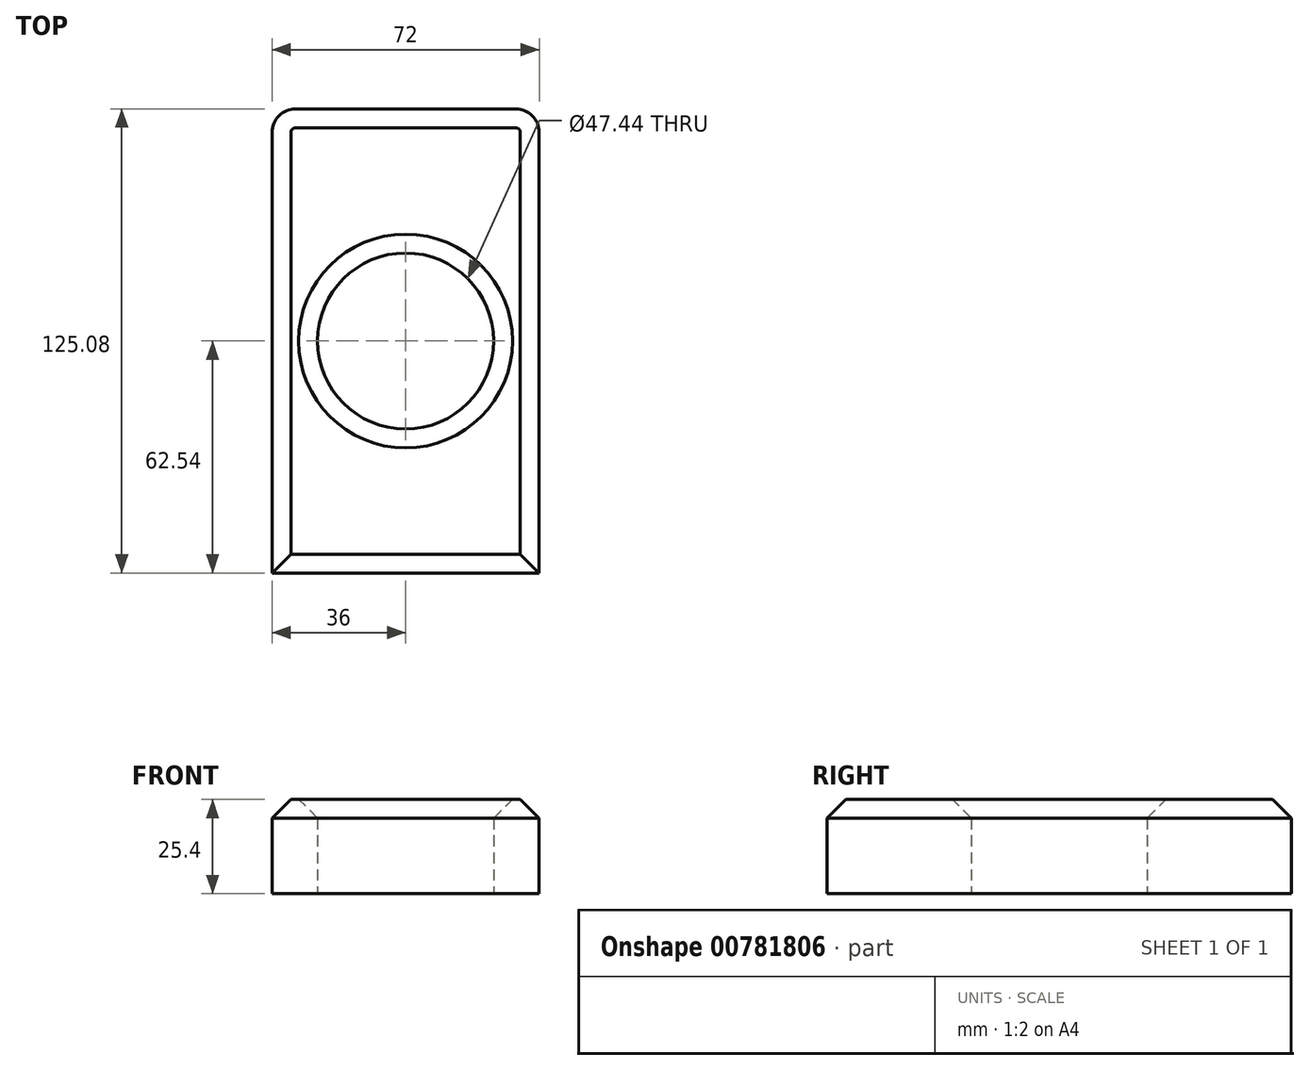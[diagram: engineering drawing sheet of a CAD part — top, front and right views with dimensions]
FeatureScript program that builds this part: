
annotation { "Feature Type Name" : "Feature", "Feature Type Description" : "" }
export const myFeature = defineFeature(function(context is Context, id is Id, definition is map)
    precondition{}
    {
        {
            var Q0;
            Q0=qCreatedBy(makeId("Top.planeOp"),FACE);
            var sketch = newSketch(context, id + "F0", { "sketchPlane" : qUnion([Q0])});
            skLineSegment(sketch, "E0.bottom", {"start": v(36, -62.54) * mm, "end": v(-36, -62.54) * mm});
            skLineSegment(sketch, "E0.top", {"start": v(29.65, 62.54) * mm, "end": v(-29.65, 62.54) * mm});
            skLineSegment(sketch, "E0.left", {"start": v(36, -62.54) * mm, "end": v(36, 56.2) * mm});
            skLineSegment(sketch, "E0.right", {"start": v(-36, -62.54) * mm, "end": v(-36, 56.2) * mm});
            skPoint(sketch, "E0.middle", {"position": v(0, 0) * mm});
            skPoint(sketch, "E1.visualSharp", {"position": v(36, 62.54) * mm});
            skArc(sketch, "E1.filletArc", {"start": v(36, 56.2) * mm, "mid": v(34.14, 60.68) * mm, "end": v(29.65, 62.54) * mm});
            skPoint(sketch, "E2.visualSharp", {"position": v(-36, 62.54) * mm});
            skArc(sketch, "E2.filletArc", {"start": v(-29.65, 62.54) * mm, "mid": v(-34.14, 60.68) * mm, "end": v(-36, 56.2) * mm});
            skCircle(sketch, "E3", {"center": v(0, 0) * mm, "radius": 23.72 * mm});
            skSolve(sketch);
        }
        {
            var Q0;
            Q0=makeQuery(id+"F0.imprint","IMPRINT",FACE,{"disambiguationData":[TD([[makeQuery(id+"F0.imprint","IMPRINT",EDGE,{"derivedFrom":sQuery(id+"F0.wireOp",EDGE,"E0.bottom")}),-1.0]])]});
            extrude(context, id + "F1", {"entities" : qUnion([Q0]), "depth" : 25.4 * mm, "offsetDistance" : 25.4 * mm});
        }
        {
            var Q0;
            Q0=makeQuery(id+"F1.opExtrude","CAP_FACE",FACE,{"disambiguationData":[OSD([sQuery(id+"F0.wireOp",EDGE,"E0.bottom"),sQuery(id+"F0.wireOp",EDGE,"E0.top"),sQuery(id+"F0.wireOp",EDGE,"E0.left"),sQuery(id+"F0.wireOp",EDGE,"E0.right"),sQuery(id+"F0.wireOp",EDGE,"E1.filletArc"),sQuery(id+"F0.wireOp",EDGE,"E2.filletArc"),sQuery(id+"F0.wireOp",EDGE,"E3")])],"isStart":false});
            chamfer(context, id + "F2", {"entities" : qUnion([Q0]), "chamferType" : ChamferType.OFFSET_ANGLE, "width" : 5.08 * mm, "oppositeDirection" : false, "angle" : 45 * degree, "tangentPropagation" : true});
        }
    });
